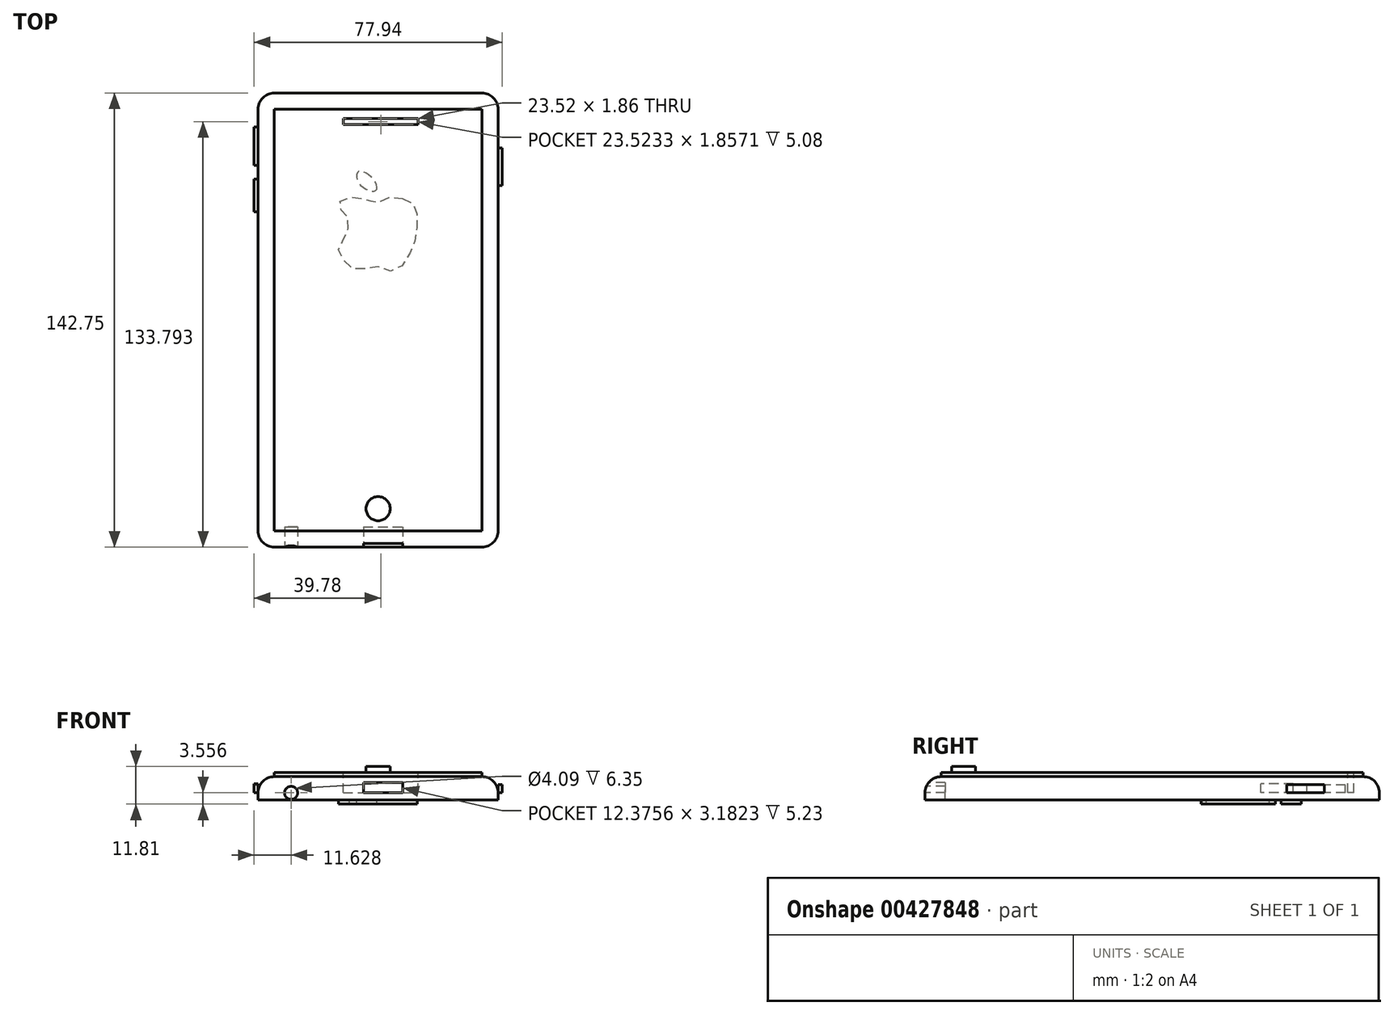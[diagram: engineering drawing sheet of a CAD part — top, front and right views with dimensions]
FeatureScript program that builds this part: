
annotation { "Feature Type Name" : "Feature", "Feature Type Description" : "" }
export const myFeature = defineFeature(function(context is Context, id is Id, definition is map)
    precondition{}
    {
        {
            var Q0;
            Q0=qCreatedBy(makeId("Top.planeOp"),FACE);
            var sketch = newSketch(context, id + "F0", { "sketchPlane" : qUnion([Q0])});
            skLineSegment(sketch, "E0.bottom", {"start": v(-63.9, 67.92) * mm, "end": v(11.51, 67.92) * mm});
            skLineSegment(sketch, "E0.top", {"start": v(-63.9, -74.83) * mm, "end": v(11.51, -74.83) * mm});
            skLineSegment(sketch, "E0.left", {"start": v(-63.9, 67.92) * mm, "end": v(-63.9, -74.83) * mm});
            skLineSegment(sketch, "E0.right", {"start": v(11.51, 67.92) * mm, "end": v(11.51, -74.83) * mm});
            skSolve(sketch);
        }
        {
            var Q0;
            Q0=makeQuery(id+"F0.imprint","IMPRINT",FACE,{"disambiguationData":[TD([[makeQuery(id+"F0.imprint","IMPRINT",EDGE,{"derivedFrom":sQuery(id+"F0.wireOp",EDGE,"E0.bottom")}),-1.0]])]});
            extrude(context, id + "F1", {"entities" : qUnion([Q0]), "depth" : 7.37 * mm});
        }
        {
            var Q0;
            Q0=makeQuery(id+"F1.opExtrude","CAP_FACE",FACE,{"disambiguationData":[OSD([sQuery(id+"F0.wireOp",EDGE,"E0.bottom"),sQuery(id+"F0.wireOp",EDGE,"E0.top"),sQuery(id+"F0.wireOp",EDGE,"E0.left"),sQuery(id+"F0.wireOp",EDGE,"E0.right")])],"isStart":false});
            var Q1;
            Q1=makeQuery(id+"F1.opExtrude","SWEPT_EDGE",EDGE,{"disambiguationData":[OSD([sQuery(id+"F0.wireOp",EDGE,"E0.top"),sQuery(id+"F0.wireOp",EDGE,"E0.left")])]});
            var Q2;
            Q2=makeQuery(id+"F1.opExtrude","SWEPT_EDGE",EDGE,{"disambiguationData":[OSD([sQuery(id+"F0.wireOp",EDGE,"E0.top"),sQuery(id+"F0.wireOp",EDGE,"E0.right")])]});
            var Q3;
            Q3=makeQuery(id+"F1.opExtrude","SWEPT_EDGE",EDGE,{"disambiguationData":[OSD([sQuery(id+"F0.wireOp",EDGE,"E0.bottom"),sQuery(id+"F0.wireOp",EDGE,"E0.left")])]});
            var Q4;
            Q4=makeQuery(id+"F1.opExtrude","SWEPT_EDGE",EDGE,{"disambiguationData":[OSD([sQuery(id+"F0.wireOp",EDGE,"E0.bottom"),sQuery(id+"F0.wireOp",EDGE,"E0.right")])]});
            fillet(context, id + "F2", {"entities" : qUnion([Q0, Q1, Q2, Q3, Q4]), "radius" : 5.08 * mm, "tangentPropagation" : true, "allowEdgeOverflow" : false});
        }
        {
            var Q0;
            Q0=makeQuery(id+"F1.opExtrude","SWEPT_FACE",FACE,{"disambiguationData":[OSD([sQuery(id+"F0.wireOp",EDGE,"E0.top")])]});
            var sketch = newSketch(context, id + "F3", { "sketchPlane" : qUnion([Q0])});
            skLineSegment(sketch, "E1.bottom", {"start": v(-30.8, 5.47) * mm, "end": v(-18.42, 5.47) * mm});
            skLineSegment(sketch, "E1.top", {"start": v(-30.8, 2.29) * mm, "end": v(-18.42, 2.29) * mm});
            skLineSegment(sketch, "E1.left", {"start": v(-30.8, 5.47) * mm, "end": v(-30.8, 2.29) * mm});
            skLineSegment(sketch, "E1.right", {"start": v(-18.42, 5.47) * mm, "end": v(-18.42, 2.29) * mm});
            skSolve(sketch);
        }
        {
            var Q0;
            Q0=makeQuery(id+"F3.imprint","IMPRINT",FACE,{"disambiguationData":[TD([[makeQuery(id+"F3.imprint","IMPRINT",EDGE,{"derivedFrom":sQuery(id+"F3.wireOp",EDGE,"E1.bottom")}),-1.0]])]});
            extrude(context, id + "F4", {"entities" : qUnion([Q0]), "operationType" : NewBodyOperationType.REMOVE, "oppositeDirection" : true, "depth" : 6.35 * mm});
        }
        {
            var Q0;
            Q0=makeQuery(id+"F1.opExtrude","SWEPT_FACE",FACE,{"disambiguationData":[OSD([sQuery(id+"F0.wireOp",EDGE,"E0.top")])]});
            var sketch = newSketch(context, id + "F5", { "sketchPlane" : qUnion([Q0])});
            skCircle(sketch, "E2", {"center": v(-53.53, 2.29) * mm, "radius": 2.05 * mm});
            skSolve(sketch);
        }
        {
            var Q0;
            Q0 = qSketchRegion(id + "F5", true);
            extrude(context, id + "F6", {"entities" : qUnion([Q0]), "operationType" : NewBodyOperationType.REMOVE, "oppositeDirection" : true, "depth" : 6.35 * mm});
        }
        {
            var Q0;
            Q0=makeQuery(id+"F1.opExtrude","CAP_FACE",FACE,{"disambiguationData":[OSD([sQuery(id+"F0.wireOp",EDGE,"E0.bottom"),sQuery(id+"F0.wireOp",EDGE,"E0.top"),sQuery(id+"F0.wireOp",EDGE,"E0.left"),sQuery(id+"F0.wireOp",EDGE,"E0.right")])],"isStart":false});
            var sketch = newSketch(context, id + "F7", { "sketchPlane" : qUnion([Q0])});
            skLineSegment(sketch, "E3.bottom", {"start": v(-58.81, 62.84) * mm, "end": v(6.43, 62.84) * mm});
            skLineSegment(sketch, "E3.top", {"start": v(-58.81, -69.75) * mm, "end": v(6.43, -69.75) * mm});
            skLineSegment(sketch, "E3.left", {"start": v(-58.81, 62.84) * mm, "end": v(-58.81, -69.75) * mm});
            skLineSegment(sketch, "E3.right", {"start": v(6.43, 62.84) * mm, "end": v(6.43, -69.75) * mm});
            skSolve(sketch);
        }
        {
            var Q0;
            Q0=makeQuery(id+"F7.imprint","IMPRINT",FACE,{"disambiguationData":[TD([[makeQuery(id+"F7.imprint","IMPRINT",EDGE,{"derivedFrom":sQuery(id+"F7.wireOp",EDGE,"E3.bottom")}),1.0]])]});
            extrude(context, id + "F8", {"entities" : qUnion([Q0]), "depth" : 1.27 * mm});
        }
        {
            var Q0;
            Q0=makeQuery(id+"F1.opExtrude","SWEPT_FACE",FACE,{"disambiguationData":[OSD([sQuery(id+"F0.wireOp",EDGE,"E0.right")])]});
            var sketch = newSketch(context, id + "F9", { "sketchPlane" : qUnion([Q0])});
            skLineSegment(sketch, "E4.bottom", {"start": v(38.85, 2.29) * mm, "end": v(50.65, 2.29) * mm});
            skLineSegment(sketch, "E4.top", {"start": v(38.85, 4.9) * mm, "end": v(50.65, 4.9) * mm});
            skLineSegment(sketch, "E4.left", {"start": v(38.85, 2.29) * mm, "end": v(38.85, 4.9) * mm});
            skLineSegment(sketch, "E4.right", {"start": v(50.65, 2.29) * mm, "end": v(50.65, 4.9) * mm});
            skSolve(sketch);
        }
        {
            var Q0;
            Q0 = qSketchRegion(id + "F9", true);
            extrude(context, id + "F10", {"entities" : qUnion([Q0]), "depth" : 1.27 * mm});
        }
        {
            var Q0;
            Q0=makeQuery(id+"F8.opExtrude","CAP_FACE",FACE,{"disambiguationData":[OSD([sQuery(id+"F7.wireOp",EDGE,"E3.bottom"),sQuery(id+"F7.wireOp",EDGE,"E3.top"),sQuery(id+"F7.wireOp",EDGE,"E3.left"),sQuery(id+"F7.wireOp",EDGE,"E3.right")])],"isStart":false});
            var sketch = newSketch(context, id + "F11", { "sketchPlane" : qUnion([Q0])});
            skCircle(sketch, "E5", {"center": v(-26.2, -62.74) * mm, "radius": 3.79 * mm});
            skPoint(sketch, "E5.centerSnap0", {"position": v(-26.2, -69.75) * mm});
            skSolve(sketch);
        }
        {
            var Q0;
            Q0 = qSketchRegion(id + "F11", true);
            extrude(context, id + "F12", {"entities" : qUnion([Q0]), "depth" : 1.9 * mm});
        }
        {
            var Q0;
            Q0=makeQuery(id+"F8.opExtrude","CAP_FACE",FACE,{"disambiguationData":[OSD([sQuery(id+"F7.wireOp",EDGE,"E3.bottom"),sQuery(id+"F7.wireOp",EDGE,"E3.top"),sQuery(id+"F7.wireOp",EDGE,"E3.left"),sQuery(id+"F7.wireOp",EDGE,"E3.right")])],"isStart":false});
            var sketch = newSketch(context, id + "F13", { "sketchPlane" : qUnion([Q0])});
            skLineSegment(sketch, "E6.bottom", {"start": v(-37.14, 59.9) * mm, "end": v(-13.62, 59.9) * mm});
            skLineSegment(sketch, "E6.top", {"start": v(-37.14, 58.03) * mm, "end": v(-13.62, 58.03) * mm});
            skLineSegment(sketch, "E6.left", {"start": v(-37.14, 59.9) * mm, "end": v(-37.14, 58.03) * mm});
            skLineSegment(sketch, "E6.right", {"start": v(-13.62, 59.9) * mm, "end": v(-13.62, 58.03) * mm});
            skSolve(sketch);
        }
        {
            var Q0;
            Q0=makeQuery(id+"F13.imprint","IMPRINT",FACE,{"disambiguationData":[TD([[makeQuery(id+"F13.imprint","IMPRINT",EDGE,{"derivedFrom":sQuery(id+"F13.wireOp",EDGE,"E6.bottom")}),-1.0]])]});
            extrude(context, id + "F14", {"entities" : qUnion([Q0]), "operationType" : NewBodyOperationType.REMOVE, "oppositeDirection" : true, "depth" : 6.35 * mm});
        }
        {
            var Q0;
            Q0=makeQuery(id+"F1.opExtrude","SWEPT_FACE",FACE,{"disambiguationData":[OSD([sQuery(id+"F0.wireOp",EDGE,"E0.left")])]});
            var sketch = newSketch(context, id + "F15", { "sketchPlane" : qUnion([Q0])});
            skLineSegment(sketch, "E7.bottom", {"start": v(-57.26, 2.29) * mm, "end": v(-45.19, 2.29) * mm});
            skLineSegment(sketch, "E7.top", {"start": v(-57.26, 4.8) * mm, "end": v(-45.19, 4.8) * mm});
            skLineSegment(sketch, "E7.left", {"start": v(-57.26, 2.29) * mm, "end": v(-57.26, 4.8) * mm});
            skLineSegment(sketch, "E7.right", {"start": v(-45.19, 2.29) * mm, "end": v(-45.19, 4.8) * mm});
            skSolve(sketch);
        }
        {
            var Q0;
            Q0=makeQuery(id+"F15.imprint","IMPRINT",FACE,{"disambiguationData":[TD([[makeQuery(id+"F15.imprint","IMPRINT",EDGE,{"derivedFrom":sQuery(id+"F15.wireOp",EDGE,"E7.bottom")}),-1.0]])]});
            extrude(context, id + "F16", {"entities" : qUnion([Q0]), "depth" : 1.27 * mm});
        }
        {
            var Q0;
            Q0=makeQuery(id+"F1.opExtrude","SWEPT_FACE",FACE,{"disambiguationData":[OSD([sQuery(id+"F0.wireOp",EDGE,"E0.left")])]});
            var sketch = newSketch(context, id + "F17", { "sketchPlane" : qUnion([Q0])});
            skLineSegment(sketch, "E8.bottom", {"start": v(-40.86, 2.29) * mm, "end": v(-30.64, 2.29) * mm});
            skLineSegment(sketch, "E8.top", {"start": v(-40.86, 5.1) * mm, "end": v(-30.64, 5.1) * mm});
            skLineSegment(sketch, "E8.left", {"start": v(-40.86, 2.29) * mm, "end": v(-40.86, 5.1) * mm});
            skLineSegment(sketch, "E8.right", {"start": v(-30.64, 2.29) * mm, "end": v(-30.64, 5.1) * mm});
            skSolve(sketch);
        }
        {
            var Q0;
            Q0=makeQuery(id+"F17.imprint","IMPRINT",FACE,{"disambiguationData":[TD([[makeQuery(id+"F17.imprint","IMPRINT",EDGE,{"derivedFrom":sQuery(id+"F17.wireOp",EDGE,"E8.bottom")}),-1.0]])]});
            extrude(context, id + "F18", {"entities" : qUnion([Q0]), "depth" : 1.27 * mm});
        }
        {
            var Q0;
            Q0=makeQuery(id+"F1.opExtrude","CAP_FACE",FACE,{"disambiguationData":[OSD([sQuery(id+"F0.wireOp",EDGE,"E0.bottom"),sQuery(id+"F0.wireOp",EDGE,"E0.top"),sQuery(id+"F0.wireOp",EDGE,"E0.left"),sQuery(id+"F0.wireOp",EDGE,"E0.right")])],"isStart":true});
            var sketch = newSketch(context, id + "F19", { "sketchPlane" : qUnion([Q0])});
            skFitSpline(sketch, "E9", {"points": [v(-26.93, -37.3) * mm, v(-27.86, -41.01) * mm, v(-32.5, -43.18) * mm, v(-31.88, -39.15) * mm, v(-26.93, -37.3) * mm]});
            skFitSpline(sketch, "E10", {"points": [v(-18.57, -34.82) * mm, v(-14.86, -32.65) * mm, v(-13.93, -28.01) * mm, v(-14.55, -21.82) * mm, v(-16.71, -16.56) * mm, v(-21.36, -11.92) * mm, v(-26.93, -13.46) * mm, v(-32.19, -12.23) * mm, v(-36.21, -14.4) * mm, v(-38.69, -18.73) * mm, v(-37.45, -21.2) * mm, v(-35.28, -27.08) * mm, v(-36.52, -29.87) * mm, v(-38.38, -32.03) * mm, v(-37.14, -34.82) * mm, v(-31.88, -34.82) * mm, v(-29.4, -34.51) * mm, v(-26.93, -33.27) * mm, v(-23.83, -34.82) * mm, v(-18.57, -34.82) * mm]});
            skSolve(sketch);
        }
        {
            var Q0;
            Q0=makeQuery(id+"F19.imprint","IMPRINT",FACE,{"disambiguationData":[TD([[makeQuery(id+"F19.imprint","IMPRINT",EDGE,{"derivedFrom":sQuery(id+"F19.wireOp",EDGE,"E9")}),-1.0]])]});
            var Q1;
            Q1=makeQuery(id+"F19.imprint","IMPRINT",FACE,{"disambiguationData":[TD([[makeQuery(id+"F19.imprint","IMPRINT",EDGE,{"derivedFrom":sQuery(id+"F19.wireOp",EDGE,"E10")}),1.0]])]});
            extrude(context, id + "F20", {"entities" : qUnion([Q0, Q1]), "depth" : 1.27 * mm});
        }
    });
